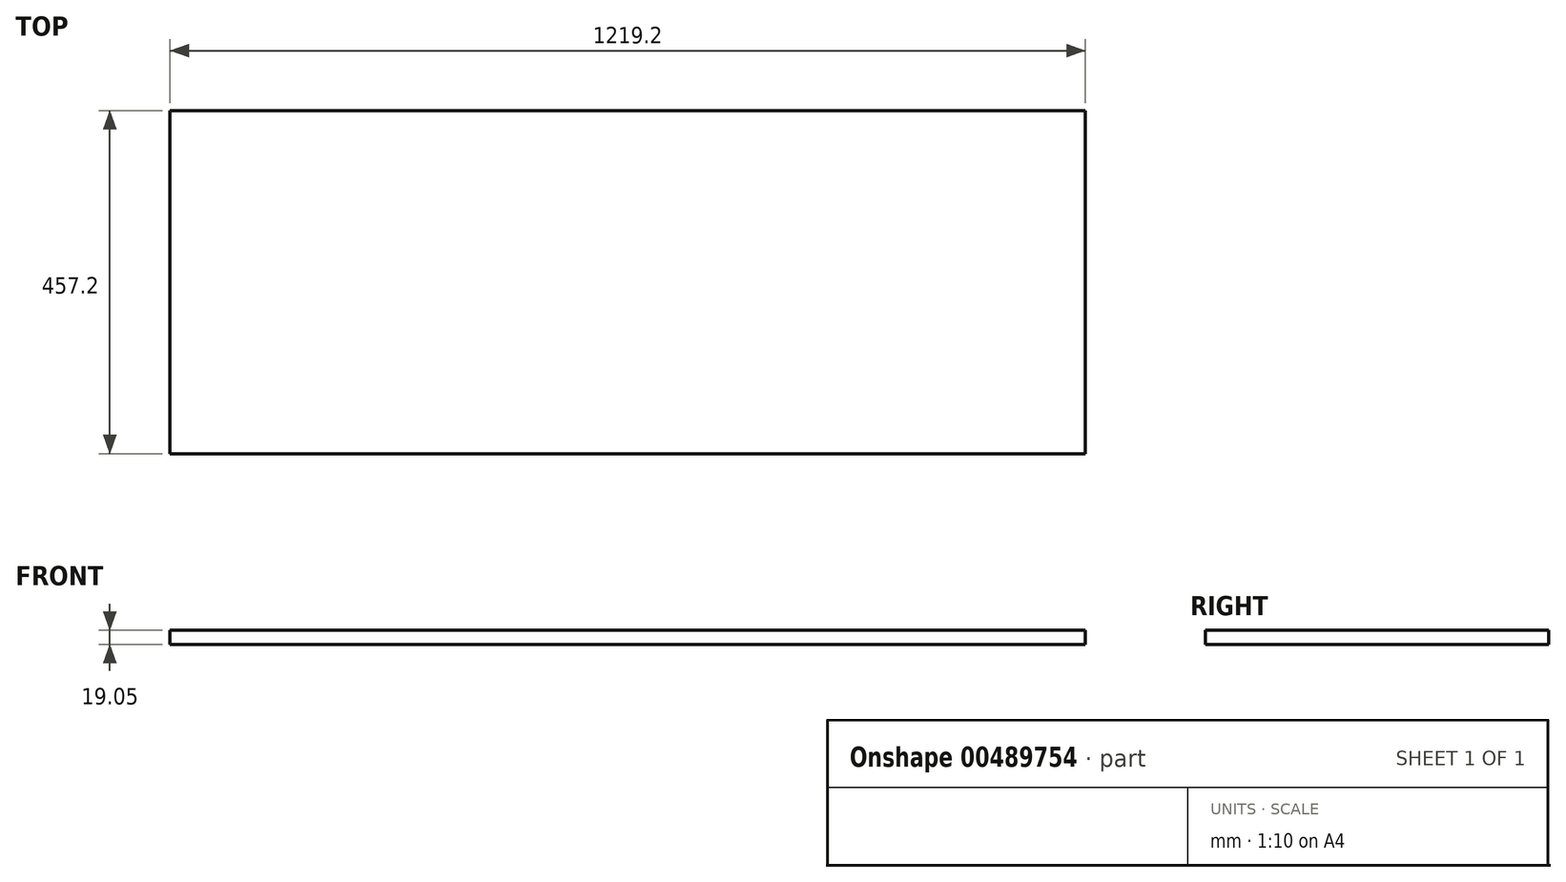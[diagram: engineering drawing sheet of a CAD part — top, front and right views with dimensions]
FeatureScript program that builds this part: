
annotation { "Feature Type Name" : "Feature", "Feature Type Description" : "" }
export const myFeature = defineFeature(function(context is Context, id is Id, definition is map)
    precondition{}
    {
        {
            var Q0;
            Q0=qCreatedBy(makeId("Top.planeOp"),FACE);
            var sketch = newSketch(context, id + "F0", { "sketchPlane" : qUnion([Q0])});
            skLineSegment(sketch, "E0.bottom", {"start": v(-610.15, -544.95) * mm, "end": v(609.05, -544.95) * mm});
            skLineSegment(sketch, "E0.top", {"start": v(-610.15, -87.75) * mm, "end": v(609.05, -87.75) * mm});
            skLineSegment(sketch, "E0.left", {"start": v(-610.15, -544.95) * mm, "end": v(-610.15, -87.75) * mm});
            skLineSegment(sketch, "E0.right", {"start": v(609.05, -544.95) * mm, "end": v(609.05, -87.75) * mm});
            skSolve(sketch);
        }
        {
            var Q0;
            Q0=makeQuery(id+"F0.imprint","IMPRINT",FACE,{"disambiguationData":[TD([[makeQuery(id+"F0.imprint","IMPRINT",EDGE,{"derivedFrom":sQuery(id+"F0.wireOp",EDGE,"E0.bottom")}),1.0]])]});
            extrude(context, id + "F1", {"entities" : qUnion([Q0]), "oppositeDirection" : true, "depth" : 19.05 * mm});
        }
    });
